FCSTD DOCUMENT  (FreeCAD 1.0R39319 (Git))
Label: Week2sketch8
License: All rights reserved
LicenseURL: https://en.wikipedia.org/wiki/All_rights_reserved
objects: Sketcher::SketchObject×1, PartDesign::Body×1
note: 3 computed .brp shape members not serialized (recipe doc carries the construction recipe); baked Part::Feature solids carry a one-line shape summary decoded from their .brp

FEATURE [Sketcher::SketchObject] Sketch
  ArcFitTolerance = 1e-06
  AttachmentSupport = -> [XY_Plane]
  FullyConstrained = true
  MakeInternals = false
  MapMode = 5
  sketch-geometry (14):
    g0: Circle CenterX=0 CenterY=0 CenterZ=0 NormalX=0 NormalY=0 NormalZ=1 AngleXU=0 Radius=30
    g1: Circle [constr] CenterX=0 CenterY=0 CenterZ=0 NormalX=0 NormalY=0 NormalZ=1 AngleXU=0 Radius=20
    g2: Circle CenterX=-40 CenterY=-70 CenterZ=0 NormalX=0 NormalY=0 NormalZ=1 AngleXU=0 Radius=15
    g3: Circle CenterX=-40 CenterY=-70 CenterZ=0 NormalX=0 NormalY=0 NormalZ=1 AngleXU=0 Radius=10
    g4: LineSegment StartX=-28.3617 StartY=9.77813 StartZ=0 EndX=-54.1809 EndY=-65.1109 EndZ=0
    g5: LineSegment StartX=28.3617 StartY=9.77813 StartZ=0 EndX=54.1809 EndY=-65.1109 EndZ=0
    g6: Circle CenterX=40 CenterY=-70 CenterZ=0 NormalX=0 NormalY=0 NormalZ=1 AngleXU=0 Radius=15
    g7: Circle CenterX=40 CenterY=-70 CenterZ=0 NormalX=0 NormalY=0 NormalZ=1 AngleXU=0 Radius=10
    g8: ArcOfCircle CenterX=0 CenterY=-90.6155 CenterZ=0 NormalX=0 NormalY=0 NormalZ=1 AngleXU=0 Radius=30 StartAngle=0.475882 EndAngle=2.66571
    g9: Circle CenterX=0 CenterY=0 CenterZ=0 NormalX=0 NormalY=0 NormalZ=1 AngleXU=0 Radius=8
    g10: Circle CenterX=0 CenterY=20 CenterZ=0 NormalX=0 NormalY=0 NormalZ=1 AngleXU=0 Radius=5
    g11: Circle CenterX=-20 CenterY=0 CenterZ=0 NormalX=0 NormalY=0 NormalZ=1 AngleXU=0 Radius=5
    g12: Circle CenterX=0 CenterY=-20 CenterZ=0 NormalX=0 NormalY=0 NormalZ=1 AngleXU=0 Radius=5
    g13: Circle CenterX=20 CenterY=0 CenterZ=0 NormalX=0 NormalY=0 NormalZ=1 AngleXU=0 Radius=5
  constraints (36):
    c: Coincident(g0,g-1)
    c: Diameter(g0) = 60
    c: Coincident(g1,g0)
    c: Diameter(g1) = 40
    c: Coincident(g3,g2)
    c: Diameter(g3) = 20
    c: Diameter(g2) = 30
    c: DistanceX(g2,g-1) = 40
    c: Distance(g2,g-1) = 70
    c: Tangent(g4,g0) = -1.5708
    c: Tangent(g4,g2) = -1.5708
    c: Coincident(g7,g6)
    c: Diameter(g7) = 20
    c: Diameter(g6) = 30
    c: Tangent(g5,g6) = 1.5708
    c: Block(g5)
    c: Block(g6)
    c: Block(g7)
    c: PointOnObject(g8,g-2)
    c: Diameter(g8) = 60
    c: PointOnObject(g8,g2)
    c: Tangent(g8,g6) = 1.5708
    c: Coincident(g9,g0)
    c: Diameter(g9) = 16
    c: PointOnObject(g10,g1)
    c: PointOnObject(g10,g-2)
    c: Diameter(g10) = 10
    c: Diameter(g11) = 10
    c: Diameter(g12) = 10
    c: Diameter(g13) = 10
    c: PointOnObject(g11,g1)
    c: PointOnObject(g11,g-1)
    c: PointOnObject(g12,g1)
    c: PointOnObject(g12,g-2)
    c: PointOnObject(g13,g1)
    c: PointOnObject(g13,g-1)
FEATURE [PartDesign::Body] Body
  AllowCompound = false
  Group = -> [Sketch]
  Origin = -> Origin
